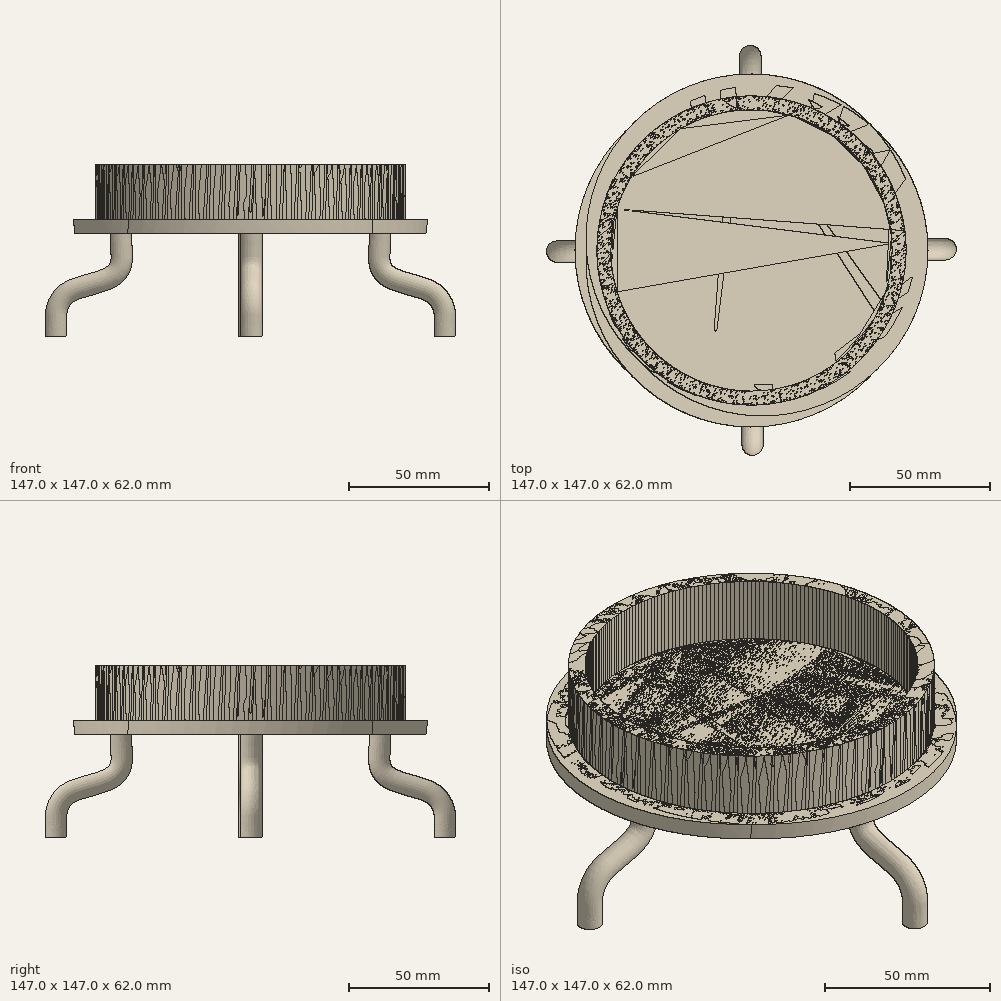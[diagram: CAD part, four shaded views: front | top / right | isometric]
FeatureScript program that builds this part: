
annotation { "Feature Type Name" : "Feature", "Feature Type Description" : "" }
export const myFeature = defineFeature(function(context is Context, id is Id, definition is map)
    precondition{}
    {
        {
            var Q0;
            Q0=qCreatedBy(makeId("Top.planeOp"),FACE);
            var sketch = newSketch(context, id + "F0", { "sketchPlane" : qUnion([Q0])});
            skCircle(sketch, "E0", {"center": v(0, 0) * mm, "radius": 50.44 * mm});
            skCircle(sketch, "E1.0", {"center": v(0, 0) * mm, "radius": 55.44 * mm});
            skSolve(sketch);
        }
        {
            var Q0;
            Q0=makeQuery(id+"F0.imprint","IMPRINT",FACE,{"disambiguationData":[TD([[makeQuery(id+"F0.imprint","IMPRINT",EDGE,{"derivedFrom":sQuery(id+"F0.wireOp",EDGE,"E0")}),-1.0]])]});
            extrude(context, id + "F1", {"entities" : qUnion([Q0]), "depth" : 20 * mm, "offsetDistance" : 25 * mm});
        }
        {
            var Q0;
            Q0=makeQuery(id+"F1.opExtrude","CAP_FACE",FACE,{"disambiguationData":[OSD([sQuery(id+"F0.wireOp",EDGE,"E0"),sQuery(id+"F0.wireOp",EDGE,"E1.0")])],"isStart":true});
            var sketch = newSketch(context, id + "F2", { "sketchPlane" : qUnion([Q0])});
            skCircle(sketch, "E2", {"center": v(0, -3.95) * mm, "radius": 59.34 * mm});
            skSolve(sketch);
        }
        {
            var Q0;
            Q0 = qSketchRegion(id + "F2", true);
            extrude(context, id + "F3", {"entities" : qUnion([Q0]), "operationType" : NewBodyOperationType.ADD, "depth" : 5 * mm, "offsetDistance" : 25 * mm});
        }
        {
            var Q0;
            Q0=qCreatedBy(makeId("Front.planeOp"),FACE);
            var sketch = newSketch(context, id + "F4", { "sketchPlane" : qUnion([Q0])});
            skFitSpline(sketch, "E3", {"points": [v(46.33, -5.56) * mm, v(46, -14.46) * mm, v(49.12, -20.22) * mm, v(59.5, -24) * mm, v(66.17, -27.05) * mm, v(69.2, -32.1) * mm, v(69.43, -36.9) * mm, v(69.43, -40.13) * mm, v(69.43, -42.9) * mm, v(69.56, -48.3) * mm], "startDerivative": vector(0.16, -50.57) * mm, "endDerivative": vector(0, -60.7) * mm});
            skSolve(sketch);
        }
        {
            var Q0;
            Q0=makeQuery(id+"F3.opExtrude","CAP_FACE",FACE,{"disambiguationData":[OSD([sQuery(id+"F2.wireOp",EDGE,"E2")])],"isStart":false});
            var sketch = newSketch(context, id + "F5", { "sketchPlane" : qUnion([Q0])});
            skCircle(sketch, "E4", {"center": v(46.54, -0.4) * mm, "radius": 3.83 * mm});
            skSolve(sketch);
        }
        {
            var Q0;
            Q0=makeQuery(id+"F5.imprint","IMPRINT",FACE,{"disambiguationData":[TD([[makeQuery(id+"F5.imprint","IMPRINT",EDGE,{"derivedFrom":sQuery(id+"F5.wireOp",EDGE,"E4")}),1.0]])]});
            var Q1;
            Q1=sQuery(id+"F4.wireOp",EDGE,"E3");
            sweep(context, id + "F6", {"operationType" : NewBodyOperationType.ADD, "profiles" : qUnion([Q0]), "path" : qUnion([Q1])});
        }
        {
            var Q0;
            Q0=qCreatedBy(makeId("Front.planeOp"),FACE);
            var sketch = newSketch(context, id + "F7", { "sketchPlane" : qUnion([Q0])});
            skLineSegment(sketch, "E5", {"start": v(0, 0) * mm, "end": v(0, -54.75) * mm});
            skSolve(sketch);
        }
        {
            var Q0;
            Q0=makeQuery(id+"F1.opExtrude","SWEPT_BODY",BODY,{"disambiguationData":[OSD([sQuery(id+"F0.wireOp",EDGE,"E0"),sQuery(id+"F0.wireOp",EDGE,"E1.0")])]});
            var Q1;
            Q1=sQuery(id+"F7.wireOp",EDGE,"E5");
            circularPattern(context, id + "F8", {"entities" : qUnion([Q0]), "axis" : qUnion([Q1]), "angle" : 360 * degree, "instanceCount" : 4, "equalSpace" : true});
        }
        {
            var Q0;
            Q0=qCreatedBy(makeId("Front.planeOp"),FACE);
            var sketch = newSketch(context, id + "F9", { "sketchPlane" : qUnion([Q0])});
            skLineSegment(sketch, "E6", {"start": v(136.08, -42.48) * mm, "end": v(-159.12, -42.48) * mm});
            skLineSegment(sketch, "E7", {"start": v(136.08, -42.48) * mm, "end": v(136.08, -78.96) * mm});
            skLineSegment(sketch, "E8", {"start": v(136.08, -78.96) * mm, "end": v(-159.12, -78.96) * mm});
            skLineSegment(sketch, "E9", {"start": v(-159.12, -78.96) * mm, "end": v(-159.12, -42.48) * mm});
            skSolve(sketch);
        }
        {
            var Q0;
            Q0 = qSketchRegion(id + "F9", true);
            extrude(context, id + "F10", {"entities" : qUnion([Q0]), "operationType" : NewBodyOperationType.REMOVE, "oppositeDirection" : true, "depth" : 96 * mm, "offsetDistance" : 25 * mm});
        }
        {
            var Q0;
            Q0 = qSketchRegion(id + "F9", true);
            extrude(context, id + "F11", {"entities" : qUnion([Q0]), "operationType" : NewBodyOperationType.REMOVE, "depth" : 103 * mm, "offsetDistance" : 25 * mm});
        }
        {
            var Q0;
            Q0=qCreatedBy(makeId("Front.planeOp"),FACE);
            cPlane(context, id + "F12", {"entities" : qUnion([Q0]), "cplaneType" : CPlaneType.OFFSET, "offset" : 108 * mm, "width" : 150 * mm, "height" : 150 * mm});
        }
        {
            var Q0;
            Q0=qCreatedBy(id+"F12.planeOp",FACE);
            var sketch = newSketch(context, id + "F13", { "sketchPlane" : qUnion([Q0])});
            skLineSegment(sketch, "E10.bottom", {"start": v(-107.03, -41.95) * mm, "end": v(105.89, -41.95) * mm});
            skLineSegment(sketch, "E10.top", {"start": v(-107.03, -93.9) * mm, "end": v(105.89, -93.9) * mm});
            skLineSegment(sketch, "E10.left", {"start": v(-107.03, -41.95) * mm, "end": v(-107.03, -93.9) * mm});
            skLineSegment(sketch, "E10.right", {"start": v(105.89, -41.95) * mm, "end": v(105.89, -93.9) * mm});
            skSolve(sketch);
        }
        {
            var Q0;
            Q0 = qSketchRegion(id + "F13", true);
            extrude(context, id + "F14", {"entities" : qUnion([Q0]), "operationType" : NewBodyOperationType.REMOVE, "oppositeDirection" : true, "depth" : 195 * mm, "offsetDistance" : 25 * mm});
        }
    });
